# Revit family: HUNTER_SOLAR-SYNC-R
name_source: partatom
category: Electrical Fixtures
revit_build: Autodesk Revit 2017 (Build: 20190508_0315(x64)
units: mm (PartAtom-declared; Revit-internal decimal feet)

## family parameters
Cut with Voids When Loaded = No
Host = Face
Maintain Annotation Orientation = No
OmniClass Number = 23.27.11.11.23
Part Type = Normal
Room Calculation Point = No
Round Connector Dimension = Use Diameter
Shared = Yes

## types (1)
- SOLAR-SYNC-R
    Assembly Code = G4030100
    Current = 3 A
    Default Elevation = 1219 mm
    Description = Solar-Sync® Wireless Receiver
    Distance Coverage = 244000 mm  [stored 800.525 ft]
    Frequency = 433000000 Hz
    Input Voltage = 24 V
    Keynote = 32 84 23.05
    Manufacturer = Hunter® Industries
    Model = SOLAR-SYNC-R
    Power = 72 VA
    Receiver Coverage Zone = Yes
    Receiver Depth = 40 mm  [stored 0.131234 ft]
    Receiver Symbol = Yes
    Receiver Width = 40 mm  [stored 0.131234 ft]
    Receiver Wiring = Wireless Solar-Sync Receiver
    Receiver height = 140 mm  [stored 0.459318 ft]
    SOLAR-SYNC® Model = SOLAR-SYNC-R
    Show Antenna = Yes
    Type Comments = SOLAR-SYNC-R® Receiver
    URL = https://www.hunterindustries.com
    Wireless Antenna = Wireless

note: [stored X ft] marks values corroborated as IEEE doubles in the binary element streams (Revit-internal decimal feet)

## geometry (parser evidence)
native form markers: Sweep x7
no freeform markers — native parametric forms only
